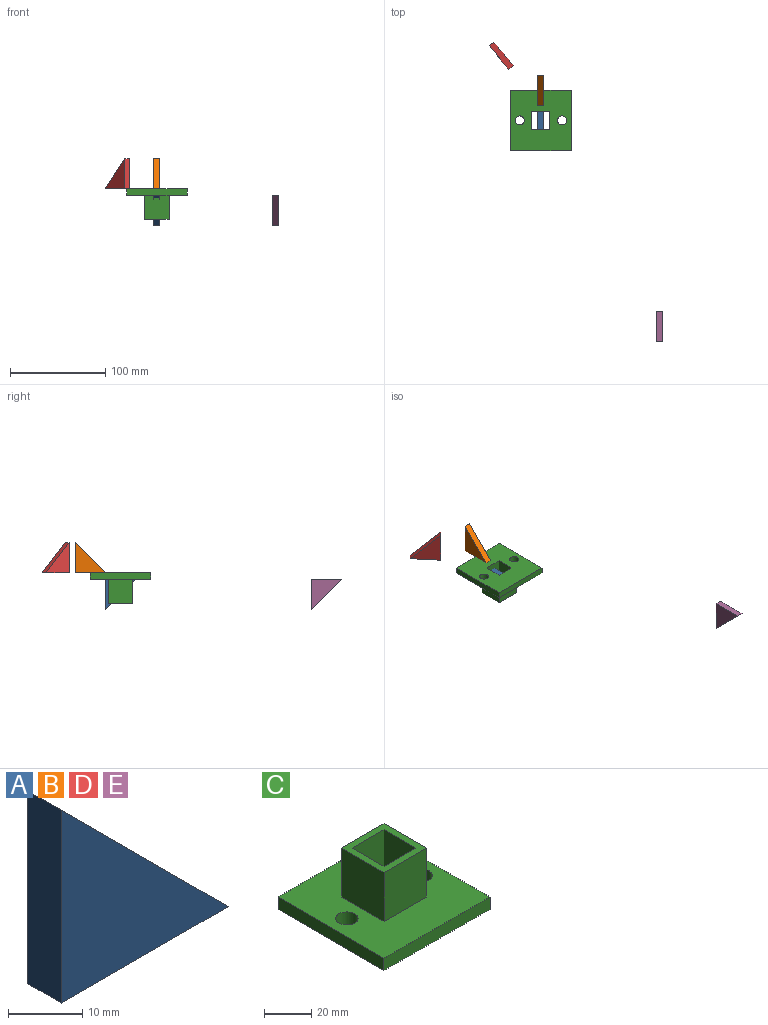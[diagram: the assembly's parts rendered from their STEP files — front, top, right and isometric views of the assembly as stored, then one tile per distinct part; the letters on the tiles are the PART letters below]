
ASSEMBLY  parts=5 mates=2
PART A: 5 faces, bbox 31.8x6.4x31.8 mm
  f0: plane 31.75x6.35mm, normal (-1,0,0), area 201.6mm2, adj f1,f2,f3,f4
  f1: plane 31.75x6.35mm, normal (0,0,-1), area 201.6mm2, adj f0,f2,f3,f4
  f2: plane 31.75x31.75mm, normal (0.71,0,0.71), area 285.1mm2, adj f0,f1,f3,f4
  f3: plane 31.75x31.75mm, normal (0,-1,0), area 504mm2, adj f0,f1,f2
  f4: plane 31.75x31.75mm, normal (0,1,0), area 504mm2, adj f0,f1,f2
PART B: same geometry as A
PART C: 17 faces, bbox 63.5x63.5x31.8 mm
  f0: plane 63.5x63.5mm, normal (0,0,1), area 3244.6mm2, adj f4,f5,f6,f7,f8,f9,f12,f13
  f1: plane 31.75x19.05mm, normal (0,-1,0), area 604.8mm2, adj f2,f10,f11,f16
  f2: plane 31.75x19.05mm, normal (-1,0,0), area 604.8mm2, adj f1,f3,f11,f16
  f3: plane 31.75x19.05mm, normal (0,1,0), area 604.8mm2, adj f2,f10,f11,f16
  f4: plane 63.5x6.35mm, normal (1,0,0), area 403.2mm2, adj f0,f5,f9,f11
  f5: plane 63.5x6.35mm, normal (0,1,0), area 403.2mm2, adj f0,f4,f6,f11
  f6: plane 63.5x6.35mm, normal (-1,0,0), area 403.2mm2, adj f0,f5,f9,f11
  f7: cylinder r=4.76mm len=9.53mm, axis (0,0,1), area 190mm2, adj f0,f11
  f8: cylinder r=4.76mm len=9.53mm, axis (0,0,1), area 190mm2, adj f0,f11
  f9: plane 63.5x6.35mm, normal (0,-1,0), area 403.2mm2, adj f0,f4,f6,f11
  f10: plane 31.75x19.05mm, normal (1,0,0), area 604.8mm2, adj f1,f3,f11,f16
  f11: plane 63.5x63.5mm, normal (0,0,-1), area 3526.8mm2, adj f1,f2,f3,f4,f5,f6,f7,f8
  f12: plane 25.4x25.4mm, normal (0,1,0), area 645.2mm2, adj f0,f13,f15,f16
  f13: plane 25.4x25.4mm, normal (-1,0,0), area 645.2mm2, adj f0,f12,f14,f16
  f14: plane 25.4x25.4mm, normal (0,-1,0), area 645.2mm2, adj f0,f13,f15,f16
  f15: plane 25.4x25.4mm, normal (1,0,0), area 645.2mm2, adj f0,f12,f14,f16
  f16: plane 25.4x25.4mm, normal (0,0,1), area 282.3mm2, adj f1,f2,f3,f10,f12,f13,f14,f15
PART D: same geometry as A
PART E: same geometry as A
PLACE A rot(axis=(0.58,0.58,-0.58),120deg) t=(3.18,23.53,-59.18)mm
PLACE B rot(axis=(0,0,-1),90deg) t=(3.17,-5.21,-7.65)mm
PLACE C rot(axis=(-1,0,0),180deg) t=(0,0,-6.35)mm
PLACE D rot(axis=(0,0,1),130deg) t=(-67.79,94.37,-7.65)mm
PLACE E rot(axis=(0.58,0.58,-0.58),120deg) t=(127.88,-193.07,-59.18)mm
MATE planar E.f0 <-> C.f0  axis (0,0,1) through (127.88,-216.6,-6.35)mm
MATE planar A.f0 <-> C.f0  axis (0,0,1) through (0,0,-6.35)mm
